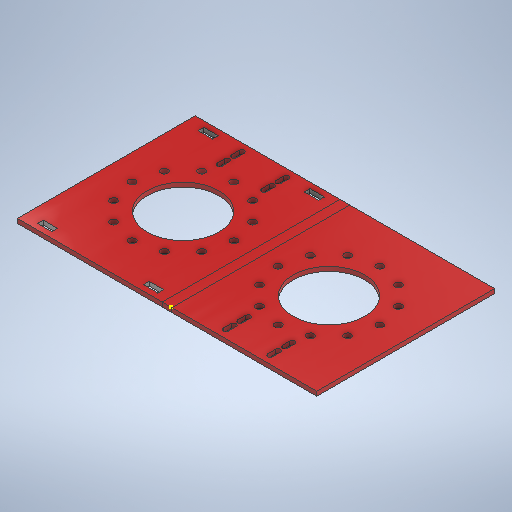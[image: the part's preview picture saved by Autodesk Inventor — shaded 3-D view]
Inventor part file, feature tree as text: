
AUTODESK INVENTOR PART (.ipt)
format: ipt  version: 2025 (Build 290162000, 162)  size: 395,264 bytes
history: native  units: mm
features: other x3, sheet_metal_op x1, sketch x1
ambient origin geometry x8: Origin, YZ Plane, XZ Plane, XY Plane, X Axis, Y Axis, Z Axis, Center Point
bodies: Solid1 (feature_tree)
feature tree (5):
  other  "Face with Harmonic Drive.ipt"
  sheet_metal_op  "Unfold1"
  sketch  "Sketch1"  dims[d0=10.0mm d1=3.0mm]
  other  "Solid1::Face with Harmonic Drive.ipt"
  other  "TaggingFeature1"
